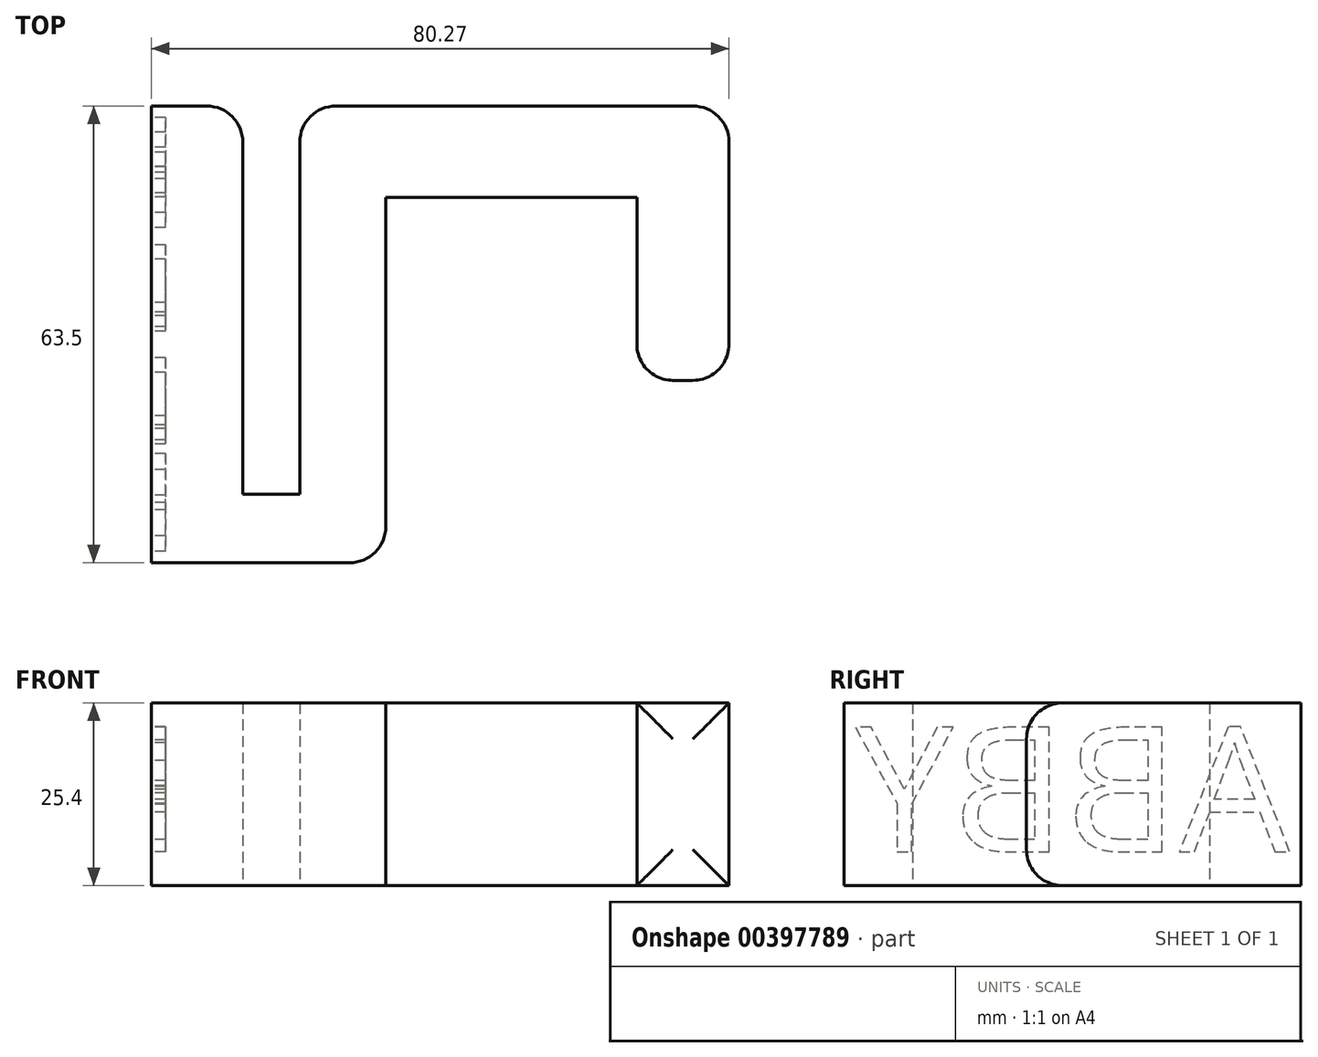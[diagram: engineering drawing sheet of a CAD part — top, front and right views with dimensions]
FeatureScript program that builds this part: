
annotation { "Feature Type Name" : "Feature", "Feature Type Description" : "" }
export const myFeature = defineFeature(function(context is Context, id is Id, definition is map)
    precondition{}
    {
        {
            var Q0;
            Q0=qCreatedBy(makeId("Top.planeOp"),FACE);
            var sketch = newSketch(context, id + "F0", { "sketchPlane" : qUnion([Q0])});
            skLineSegment(sketch, "E0", {"start": v(0, 0) * mm, "end": v(0, 63.5) * mm});
            skLineSegment(sketch, "E1", {"start": v(0, 63.5) * mm, "end": v(12.7, 63.5) * mm});
            skLineSegment(sketch, "E2", {"start": v(12.7, 63.5) * mm, "end": v(12.7, 9.53) * mm});
            skLineSegment(sketch, "E3", {"start": v(12.7, 9.53) * mm, "end": v(20.64, 9.53) * mm});
            skLineSegment(sketch, "E4", {"start": v(20.64, 9.53) * mm, "end": v(20.64, 63.5) * mm});
            skLineSegment(sketch, "E5", {"start": v(20.64, 63.5) * mm, "end": v(80.27, 63.5) * mm});
            skLineSegment(sketch, "E6", {"start": v(80.27, 63.5) * mm, "end": v(80.27, 25.35) * mm});
            skLineSegment(sketch, "E7", {"start": v(80.27, 25.35) * mm, "end": v(67.48, 25.35) * mm});
            skLineSegment(sketch, "E8", {"start": v(67.48, 25.35) * mm, "end": v(67.48, 50.8) * mm});
            skLineSegment(sketch, "E9", {"start": v(67.48, 50.8) * mm, "end": v(32.58, 50.8) * mm});
            skLineSegment(sketch, "E10", {"start": v(32.58, 50.8) * mm, "end": v(32.58, 0) * mm});
            skLineSegment(sketch, "E11", {"start": v(32.58, 0) * mm, "end": v(0, 0) * mm});
            skSolve(sketch);
        }
        {
            var Q0;
            Q0=makeQuery(id+"F0.imprint","IMPRINT",FACE,{"disambiguationData":[TD([[makeQuery(id+"F0.imprint","IMPRINT",EDGE,{"derivedFrom":sQuery(id+"F0.wireOp",EDGE,"E0")}),-1.0]])]});
            extrude(context, id + "F1", {"entities" : qUnion([Q0]), "depth" : 25.4 * mm});
        }
        {
            var Q0;
            Q0=makeQuery(id+"F1.opExtrude","CAP_EDGE",EDGE,{"disambiguationData":[OSD([sQuery(id+"F0.wireOp",EDGE,"E7")])],"isStart":false});
            var Q1;
            Q1=makeQuery(id+"F1.opExtrude","CAP_EDGE",EDGE,{"disambiguationData":[OSD([sQuery(id+"F0.wireOp",EDGE,"E7")])],"isStart":true});
            var Q2;
            Q2=makeQuery(id+"F1.opExtrude","SWEPT_EDGE",EDGE,{"disambiguationData":[OSD([sQuery(id+"F0.wireOp",EDGE,"E6"),sQuery(id+"F0.wireOp",EDGE,"E7")])]});
            var Q3;
            Q3=makeQuery(id+"F1.opExtrude","SWEPT_EDGE",EDGE,{"disambiguationData":[OSD([sQuery(id+"F0.wireOp",EDGE,"E7"),sQuery(id+"F0.wireOp",EDGE,"E8")])]});
            var Q4;
            Q4=makeQuery(id+"F1.opExtrude","SWEPT_EDGE",EDGE,{"disambiguationData":[OSD([sQuery(id+"F0.wireOp",EDGE,"E5"),sQuery(id+"F0.wireOp",EDGE,"E6")])]});
            var Q5;
            Q5=makeQuery(id+"F1.opExtrude","SWEPT_EDGE",EDGE,{"disambiguationData":[OSD([sQuery(id+"F0.wireOp",EDGE,"E10"),sQuery(id+"F0.wireOp",EDGE,"E11")])]});
            var Q6;
            Q6=makeQuery(id+"F1.opExtrude","SWEPT_EDGE",EDGE,{"disambiguationData":[OSD([sQuery(id+"F0.wireOp",EDGE,"E4"),sQuery(id+"F0.wireOp",EDGE,"E5")])]});
            var Q7;
            Q7=makeQuery(id+"F1.opExtrude","SWEPT_EDGE",EDGE,{"disambiguationData":[OSD([sQuery(id+"F0.wireOp",EDGE,"E1"),sQuery(id+"F0.wireOp",EDGE,"E2")])]});
            fillet(context, id + "F2", {"entities" : qUnion([Q0, Q1, Q2, Q3, Q4, Q5, Q6, Q7]), "radius" : 5 * mm, "tangentPropagation" : true, "allowEdgeOverflow" : false});
        }
        {
            var Q0;
            Q0=makeQuery(id+"F1.opExtrude","SWEPT_FACE",FACE,{"disambiguationData":[OSD([sQuery(id+"F0.wireOp",EDGE,"E0")])]});
            var sketch = newSketch(context, id + "F3", { "sketchPlane" : qUnion([Q0])});
            skText(sketch, "E12", { "text": "ABBY", "fontName": "OpenSans-Regular.ttf"});
            const initialGuessF3  = {"E12": [-0.06194, 0.00472, 1, 0, 0.01746]};
            skSetInitialGuess(sketch, initialGuessF3);
            skSolve(sketch);
        }
        {
            var Q0;
            Q0 = qSketchRegion(id + "F3", true);
            var Q1;
            Q1 = qConstructionFilter(qBodyType(qCreatedBy(id + "F3" ,EDGE), BodyType.WIRE), ConstructionObject.NO);
            extrude(context, id + "F4", {"entities" : qUnion([Q0]), "operationType" : NewBodyOperationType.REMOVE, "surfaceEntities" : qUnion([Q1]), "oppositeDirection" : true, "depth" : 2 * mm, "offsetDistance" : 25 * mm});
        }
    });
